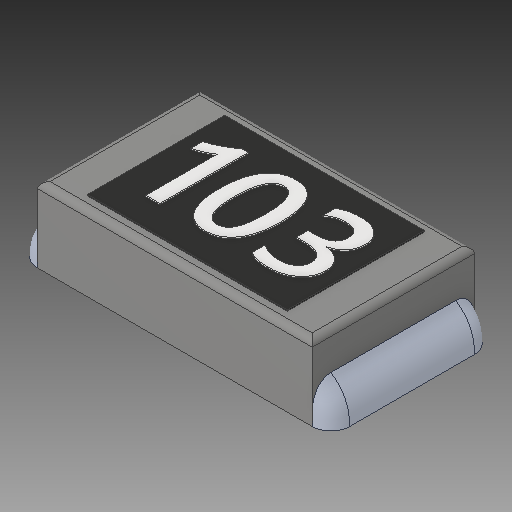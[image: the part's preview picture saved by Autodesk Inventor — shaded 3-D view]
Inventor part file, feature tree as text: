
AUTODESK INVENTOR PART (.ipt)
format: ipt  version: 2018.3 (Build 223284000, 284)  size: 266,752 bytes
history: native  units: mm
features: other x4, fillet x1, mirror x1
ambient origin geometry x8: Origin, YZ Plane, XZ Plane, XY Plane, X Axis, Y Axis, Z Axis, Center Point
bodies: Body1 (feature_tree), Body2 (feature_tree), Body3 (feature_tree)
feature tree (6):
  other  "Sólido1"
  other  "Sólido2"
  other  "Sólido3"
  fillet  "Fillet2"  [1 undecoded]
  mirror  "Mirror1"
  other  "Boss-Extrude4"
note: 1 required parameter value undecoded (feature->parameter linkage not recoverable at this tier; creation-order binding heuristic only, values carry confidence <= 0.55)
